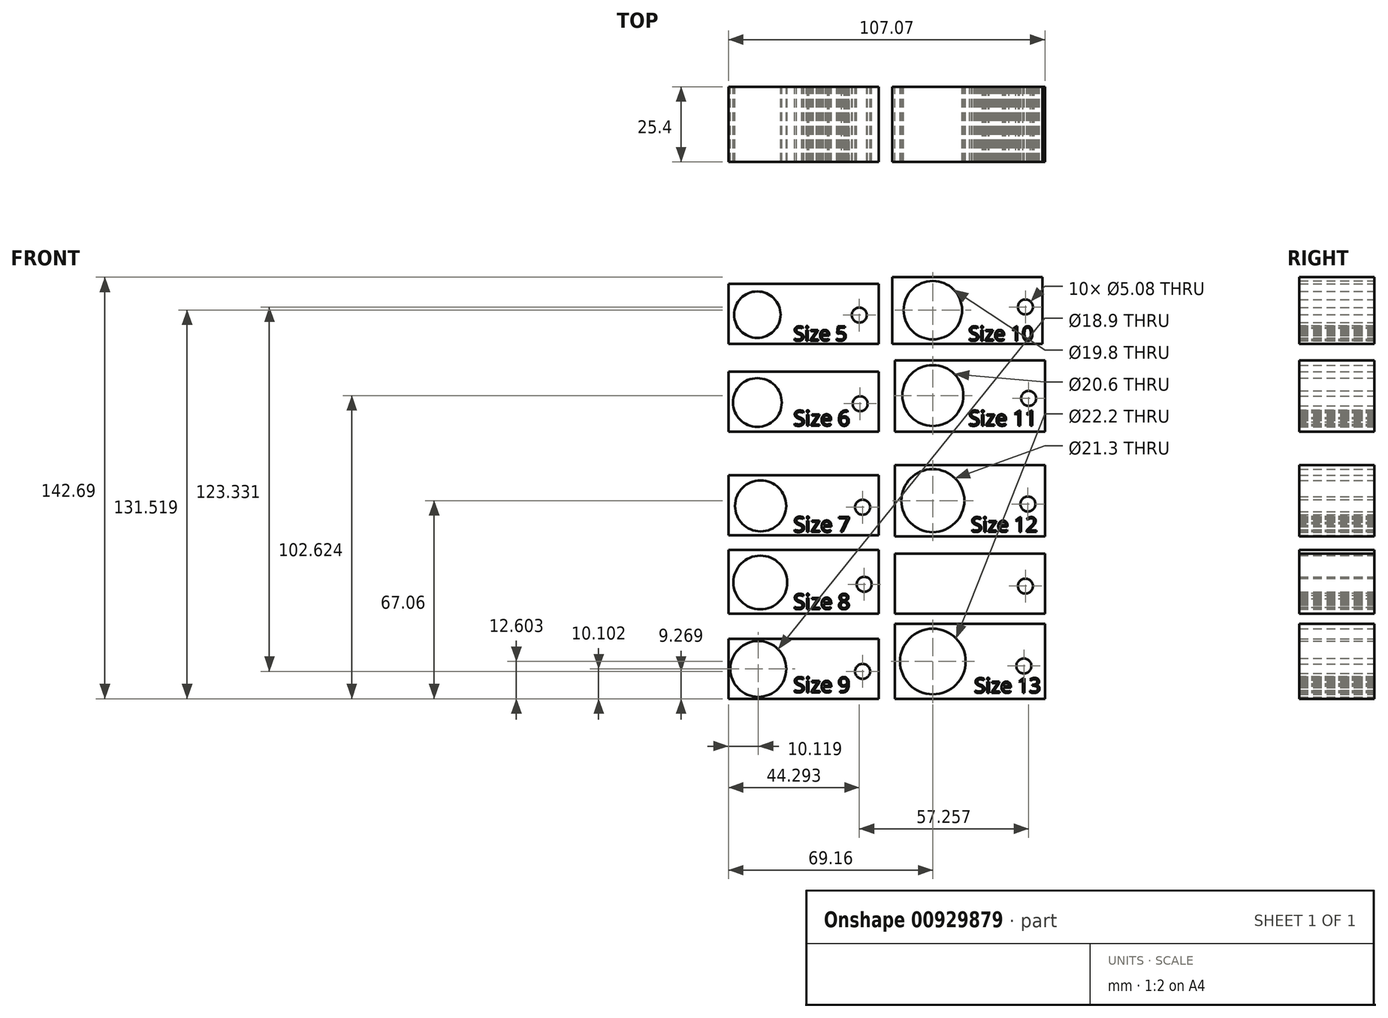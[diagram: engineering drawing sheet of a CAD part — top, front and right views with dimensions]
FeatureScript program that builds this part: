
annotation { "Feature Type Name" : "Feature", "Feature Type Description" : "" }
export const myFeature = defineFeature(function(context is Context, id is Id, definition is map)
    precondition{}
    {
        {
            var Q0;
            Q0=qCreatedBy(makeId("Front.planeOp"),FACE);
            var sketch = newSketch(context, id + "F0", { "sketchPlane" : qUnion([Q0])});
            skCircle(sketch, "E0", {"center": v(-59.35, 59.77) * mm, "radius": 7.85 * mm});
            skCircle(sketch, "E1", {"center": v(-59.35, 30.02) * mm, "radius": 8.25 * mm});
            skCircle(sketch, "E2", {"center": v(-58.25, -4.96) * mm, "radius": 8.65 * mm});
            skCircle(sketch, "E3", {"center": v(-58.35, -30.88) * mm, "radius": 9.1 * mm});
            skCircle(sketch, "E4", {"center": v(-59.04, -60.13) * mm, "radius": 9.45 * mm});
            skCircle(sketch, "E5", {"center": v(0, 61.29) * mm, "radius": 9.9 * mm});
            skCircle(sketch, "E6", {"center": v(0, 32.4) * mm, "radius": 10.3 * mm});
            skCircle(sketch, "E7", {"center": v(0, -57.63) * mm, "radius": 11.1 * mm});
            skLineSegment(sketch, "E8.bottom", {"start": v(-69.16, 70.23) * mm, "end": v(-18.36, 70.23) * mm});
            skLineSegment(sketch, "E8.top", {"start": v(-69.16, 49.9) * mm, "end": v(-18.36, 49.9) * mm});
            skLineSegment(sketch, "E8.left", {"start": v(-69.16, 70.23) * mm, "end": v(-69.16, 49.9) * mm});
            skLineSegment(sketch, "E8.right", {"start": v(-18.36, 70.23) * mm, "end": v(-18.36, 49.9) * mm});
            skLineSegment(sketch, "E9.bottom", {"start": v(-69.16, 40.54) * mm, "end": v(-18.36, 40.54) * mm});
            skLineSegment(sketch, "E9.top", {"start": v(-69.16, 20.22) * mm, "end": v(-18.36, 20.22) * mm});
            skLineSegment(sketch, "E9.left", {"start": v(-69.16, 40.54) * mm, "end": v(-69.16, 20.22) * mm});
            skLineSegment(sketch, "E9.right", {"start": v(-18.36, 40.54) * mm, "end": v(-18.36, 20.22) * mm});
            skLineSegment(sketch, "E10.bottom", {"start": v(-69.16, 5.45) * mm, "end": v(-18.36, 5.45) * mm});
            skLineSegment(sketch, "E10.top", {"start": v(-69.16, -14.87) * mm, "end": v(-18.36, -14.87) * mm});
            skLineSegment(sketch, "E10.left", {"start": v(-69.16, 5.45) * mm, "end": v(-69.16, -14.87) * mm});
            skLineSegment(sketch, "E10.right", {"start": v(-18.36, 5.45) * mm, "end": v(-18.36, -14.87) * mm});
            skLineSegment(sketch, "E11.bottom", {"start": v(-69.16, -19.89) * mm, "end": v(-18.36, -19.89) * mm});
            skLineSegment(sketch, "E11.top", {"start": v(-69.16, -41.48) * mm, "end": v(-18.36, -41.48) * mm});
            skLineSegment(sketch, "E11.left", {"start": v(-69.16, -19.89) * mm, "end": v(-69.16, -41.48) * mm});
            skLineSegment(sketch, "E11.right", {"start": v(-18.36, -19.89) * mm, "end": v(-18.36, -41.48) * mm});
            skLineSegment(sketch, "E12.bottom", {"start": v(-69.16, -49.91) * mm, "end": v(-18.36, -49.91) * mm});
            skLineSegment(sketch, "E12.top", {"start": v(-69.16, -70.23) * mm, "end": v(-18.36, -70.23) * mm});
            skLineSegment(sketch, "E12.left", {"start": v(-69.16, -49.91) * mm, "end": v(-69.16, -70.23) * mm});
            skLineSegment(sketch, "E12.right", {"start": v(-18.36, -49.91) * mm, "end": v(-18.36, -70.23) * mm});
            skLineSegment(sketch, "E13.bottom", {"start": v(-13.76, 72.46) * mm, "end": v(37.04, 72.46) * mm});
            skLineSegment(sketch, "E13.top", {"start": v(-13.76, 49.85) * mm, "end": v(37.04, 49.85) * mm});
            skLineSegment(sketch, "E13.left", {"start": v(-13.76, 72.46) * mm, "end": v(-13.76, 49.85) * mm});
            skLineSegment(sketch, "E13.right", {"start": v(37.04, 72.46) * mm, "end": v(37.04, 49.85) * mm});
            skLineSegment(sketch, "E14.bottom", {"start": v(-12.89, 44.35) * mm, "end": v(37.91, 44.35) * mm});
            skLineSegment(sketch, "E14.top", {"start": v(-12.89, 20.22) * mm, "end": v(37.91, 20.22) * mm});
            skLineSegment(sketch, "E14.left", {"start": v(-12.89, 44.35) * mm, "end": v(-12.89, 20.22) * mm});
            skLineSegment(sketch, "E14.right", {"start": v(37.91, 44.35) * mm, "end": v(37.91, 20.22) * mm});
            skLineSegment(sketch, "E15.bottom", {"start": v(-12.89, 8.82) * mm, "end": v(37.91, 8.82) * mm});
            skLineSegment(sketch, "E15.top", {"start": v(-12.89, -15.31) * mm, "end": v(37.91, -15.31) * mm});
            skLineSegment(sketch, "E15.left", {"start": v(-12.89, 8.82) * mm, "end": v(-12.89, -15.31) * mm});
            skLineSegment(sketch, "E15.right", {"start": v(37.91, 8.82) * mm, "end": v(37.91, -15.31) * mm});
            skLineSegment(sketch, "E16.bottom", {"start": v(-12.89, -21.16) * mm, "end": v(37.91, -21.16) * mm});
            skLineSegment(sketch, "E16.top", {"start": v(-12.89, -41.48) * mm, "end": v(37.91, -41.48) * mm});
            skLineSegment(sketch, "E16.left", {"start": v(-12.89, -21.16) * mm, "end": v(-12.89, -41.48) * mm});
            skLineSegment(sketch, "E16.right", {"start": v(37.91, -21.16) * mm, "end": v(37.91, -41.48) * mm});
            skLineSegment(sketch, "E17.bottom", {"start": v(-12.89, -44.83) * mm, "end": v(37.91, -44.83) * mm});
            skLineSegment(sketch, "E17.top", {"start": v(-12.89, -70.23) * mm, "end": v(37.91, -70.23) * mm});
            skLineSegment(sketch, "E17.left", {"start": v(-12.89, -44.83) * mm, "end": v(-12.89, -70.23) * mm});
            skLineSegment(sketch, "E17.right", {"start": v(37.91, -44.83) * mm, "end": v(37.91, -70.23) * mm});
            skCircle(sketch, "E18", {"center": v(0, -3.17) * mm, "radius": 10.65 * mm});
            skCircle(sketch, "E19", {"center": v(-24.87, 59.62) * mm, "radius": 2.54 * mm});
            skCircle(sketch, "E20", {"center": v(-24.59, 29.62) * mm, "radius": 2.54 * mm});
            skCircle(sketch, "E21", {"center": v(-23.76, -5.4) * mm, "radius": 2.54 * mm});
            skCircle(sketch, "E22", {"center": v(-23.2, -31.5) * mm, "radius": 2.54 * mm});
            skCircle(sketch, "E23", {"center": v(-23.76, -60.96) * mm, "radius": 2.54 * mm});
            skCircle(sketch, "E24", {"center": v(30.8, -59.14) * mm, "radius": 2.54 * mm});
            skCircle(sketch, "E25", {"center": v(31.32, -32.1) * mm, "radius": 2.54 * mm});
            skCircle(sketch, "E26", {"center": v(32.15, -4.32) * mm, "radius": 2.54 * mm});
            skCircle(sketch, "E27", {"center": v(32.39, 31.42) * mm, "radius": 2.54 * mm});
            skCircle(sketch, "E28", {"center": v(31.32, 62.37) * mm, "radius": 2.54 * mm});
            skSolve(sketch);
        }
        {
            var Q0;
            Q0=qCreatedBy(makeId("Front.planeOp"),FACE);
            var sketch = newSketch(context, id + "F1", { "sketchPlane" : qUnion([Q0])});
            skText(sketch, "E29", { "text": "Size 5", "fontName": "OpenSans-Regular.ttf"});
            skText(sketch, "E30", { "text": "Size 6\n", "fontName": "OpenSans-Regular.ttf"});
            skText(sketch, "E31", { "text": "Size 7\n", "fontName": "OpenSans-Regular.ttf"});
            skText(sketch, "E32", { "text": "Size 8\n", "fontName": "OpenSans-Regular.ttf"});
            skText(sketch, "E33", { "text": "Size 9\n", "fontName": "OpenSans-Regular.ttf"});
            skText(sketch, "E34", { "text": "Size 10", "fontName": "OpenSans-Regular.ttf"});
            skText(sketch, "E35", { "text": "Size 11\n", "fontName": "OpenSans-Regular.ttf"});
            skText(sketch, "E36", { "text": "Size 12\n", "fontName": "OpenSans-Regular.ttf"});
            skText(sketch, "E37", { "text": "Size 13", "fontName": "OpenSans-Regular.ttf"});
            const initialGuessF1  = {"E29": [-0.04713, 0.05093, 1, 0, 0.00489], "E30": [-0.04713, 0.02217, 1, 0, 0.00516], "E31": [-0.04713, -0.01378, 1, 0, 0.00517], "E32": [-0.04713, -0.0399, 1, 0, 0.00517], "E33": [-0.04713, -0.06806, 1, 0, 0.00517], "E34": [0.01205, 0.05093, 1, 0, 0.00489], "E35": [0.01205, 0.02217, 1, 0, 0.00516], "E36": [0.01292, -0.01373, 1, 0, 0.005], "E37": [0.01403, -0.0682, 1, 0, 0.005]};
            skSetInitialGuess(sketch, initialGuessF1);
            skSolve(sketch);
        }
        {
            var Q0;
            Q0 = qSketchRegion(id + "F0", true);
            extrude(context, id + "F2", {"entities" : qUnion([Q0]), "depth" : 25.4 * mm, "offsetDistance" : 25.4 * mm});
        }
        {
            var Q0;
            Q0 = qSketchRegion(id + "F1", true);
            extrude(context, id + "F3", {"entities" : qUnion([Q0]), "depth" : 25.4 * mm, "offsetDistance" : 25.4 * mm});
        }
    });
